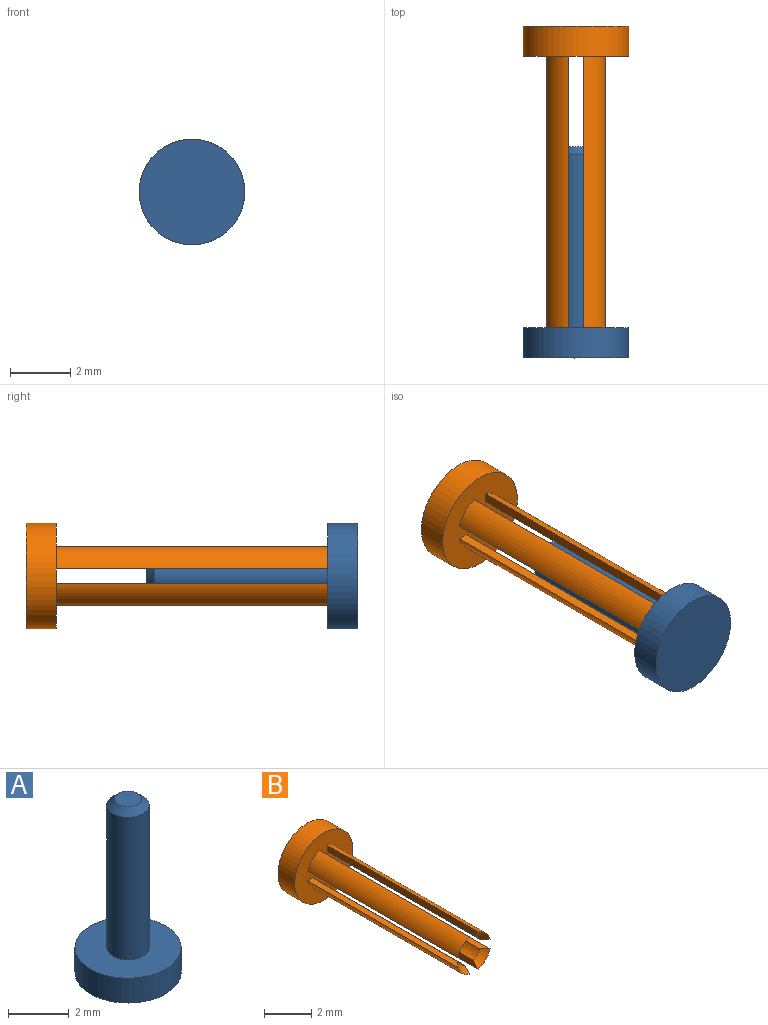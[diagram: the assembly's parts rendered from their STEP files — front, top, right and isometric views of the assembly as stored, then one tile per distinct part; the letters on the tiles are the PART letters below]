
ASSEMBLY  parts=2 mates=1
PART A: 6 faces, bbox 3.5x3.5x7 mm
  f0: cylinder r=1.75mm len=3.5mm, axis (0,0,-1), area 11mm2, adj f1,f2
  f1: plane 3.5x3.5mm, normal (0,0,1), area 8.1mm2, adj f0,f3
  f2: plane 3.5x3.5mm, normal (0,0,-1), area 9.6mm2, adj f0
  f3: cylinder r=0.7mm len=5.75mm, axis (0,0,-1), area 25.3mm2, adj f1,f5
  f4: plane 0.9x0.9mm, normal (0,0,1), area 0.6mm2, adj f5
  f5: cone r=0.45mm half-angle=45deg, axis (0,0,-1), area 1.3mm2, adj f3,f4
PART B: 23 faces, bbox 3.5x10x3.5 mm
  f0: cylinder r=1mm len=9mm, axis (0,1,0), area 9.6mm2, adj f7,f11,f17,f20
  f1: cylinder r=1mm len=9mm, axis (0,1,0), area 9.6mm2, adj f7,f16,f18,f21
  f2: cylinder r=1mm len=9mm, axis (0,1,0), area 9.6mm2, adj f7,f12,f13,f19
  f3: cylinder r=0.7mm len=8.7mm, axis (0,-1,0), area 5.1mm2, adj f7,f11,f17,f20
  f4: cylinder r=0.7mm len=8.7mm, axis (0,-1,0), area 5.1mm2, adj f7,f16,f18,f21
  f5: cylinder r=0.7mm len=8.7mm, axis (0,-1,0), area 5.1mm2, adj f7,f12,f13,f19
  f6: cylinder r=1.75mm len=3.5mm, axis (0,1,0), area 11mm2, adj f7,f8
  f7: plane 3.5x3.5mm, normal (0,-1,0), area 8.6mm2, adj f0,f1,f2,f3,f4,f5,f6,f9
  f8: plane 3.5x3.5mm, normal (0,1,0), area 9.6mm2, adj f6
  f9: cylinder r=1mm len=9mm, axis (0,1,0), area 9.6mm2, adj f7,f14,f15,f22
  f10: cylinder r=0.7mm len=8.7mm, axis (0,-1,0), area 5.1mm2, adj f7,f14,f15,f22
  f11: plane 9.02x0.33mm, normal (-1,0,0), area 2.8mm2, adj f0,f3,f7,f20
  f12: plane 9.02x0.33mm, normal (1,0,0), area 2.8mm2, adj f2,f5,f7,f19
  f13: plane 9.02x0.33mm, normal (0,0,1), area 2.8mm2, adj f2,f5,f7,f19
  f14: plane 9.02x0.33mm, normal (0,0,-1), area 2.8mm2, adj f7,f9,f10,f22
  f15: plane 9.02x0.33mm, normal (1,0,0), area 2.8mm2, adj f7,f9,f10,f22
  f16: plane 9.02x0.33mm, normal (-1,0,0), area 2.8mm2, adj f1,f4,f7,f21
  f17: plane 9.02x0.33mm, normal (0,0,1), area 2.8mm2, adj f0,f3,f7,f20
  f18: plane 9.02x0.33mm, normal (0,0,-1), area 2.8mm2, adj f1,f4,f7,f21
  f19: cone r=0.7mm half-angle=45deg, axis (0,-1,0), area 0.3mm2, adj f2,f5,f12,f13
  f20: cone r=0.7mm half-angle=45deg, axis (0,-1,0), area 0.3mm2, adj f0,f3,f11,f17
  f21: cone r=0.7mm half-angle=45deg, axis (0,-1,0), area 0.3mm2, adj f1,f4,f16,f18
  f22: cone r=0.7mm half-angle=45deg, axis (0,-1,0), area 0.3mm2, adj f9,f10,f14,f15
PLACE A rot(axis=(-1,0,0),90deg) t=(-3.34,-13.53,-1.65)mm
PLACE B t=(-3.34,-2.53,-1.65)mm
MATE fastened A.f0 <-> B.f0  axis (0,1,0) through (-3.34,-12.53,-1.65)mm
